# Revit family: Haworth_Mexique_OccasionalTable
name_source: partatom
category: Furniture
revit_build: Autodesk Revit 2018 (Build: 20170223_1515(x64)
units: mm (PartAtom-declared; Revit-internal decimal feet)

## family parameters
Always vertical = Yes
Cut with Voids When Loaded = No
OmniClass Number = 23.40.70.14.64.21
OmniClass Title = Systems Furniture
Room Calculation Point = No
Shared = No
Work Plane-Based = No

## types (3) — shared parameters
Actual Depth = 31.5 "
Actual Width = 46.5 "
Assembly Code = E2020200
Manufacturer = Haworth
Model = HCCSMXTO
Revision Number = 1
Size = Verify Final Dim. w/ Haworth
Sustainability Info = https://www.haworth.com
URL = https://www.haworth.com
URL - Product = https://www.haworth.com
Warranty = http://www.haworth.com

## per-type parameters (varying)
| type | Actual Height | Description | High | Low | Medium |
| Low Occasional Table | 12.2 " | Haworth - Cassina - Mexique - Occasional Table - Low | No | Yes | No |
| Medium Occasional Table | 15 " | Haworth - Cassina - Mexique - Occasional Table - Medium | No | No | Yes |
| High Occasional Table | 17.7 " | Haworth - Cassina - Mexique - Occasional Table - High | Yes | No | No |

## geometry (parser evidence)
native form markers: Sweep x7
no freeform markers — native parametric forms only
